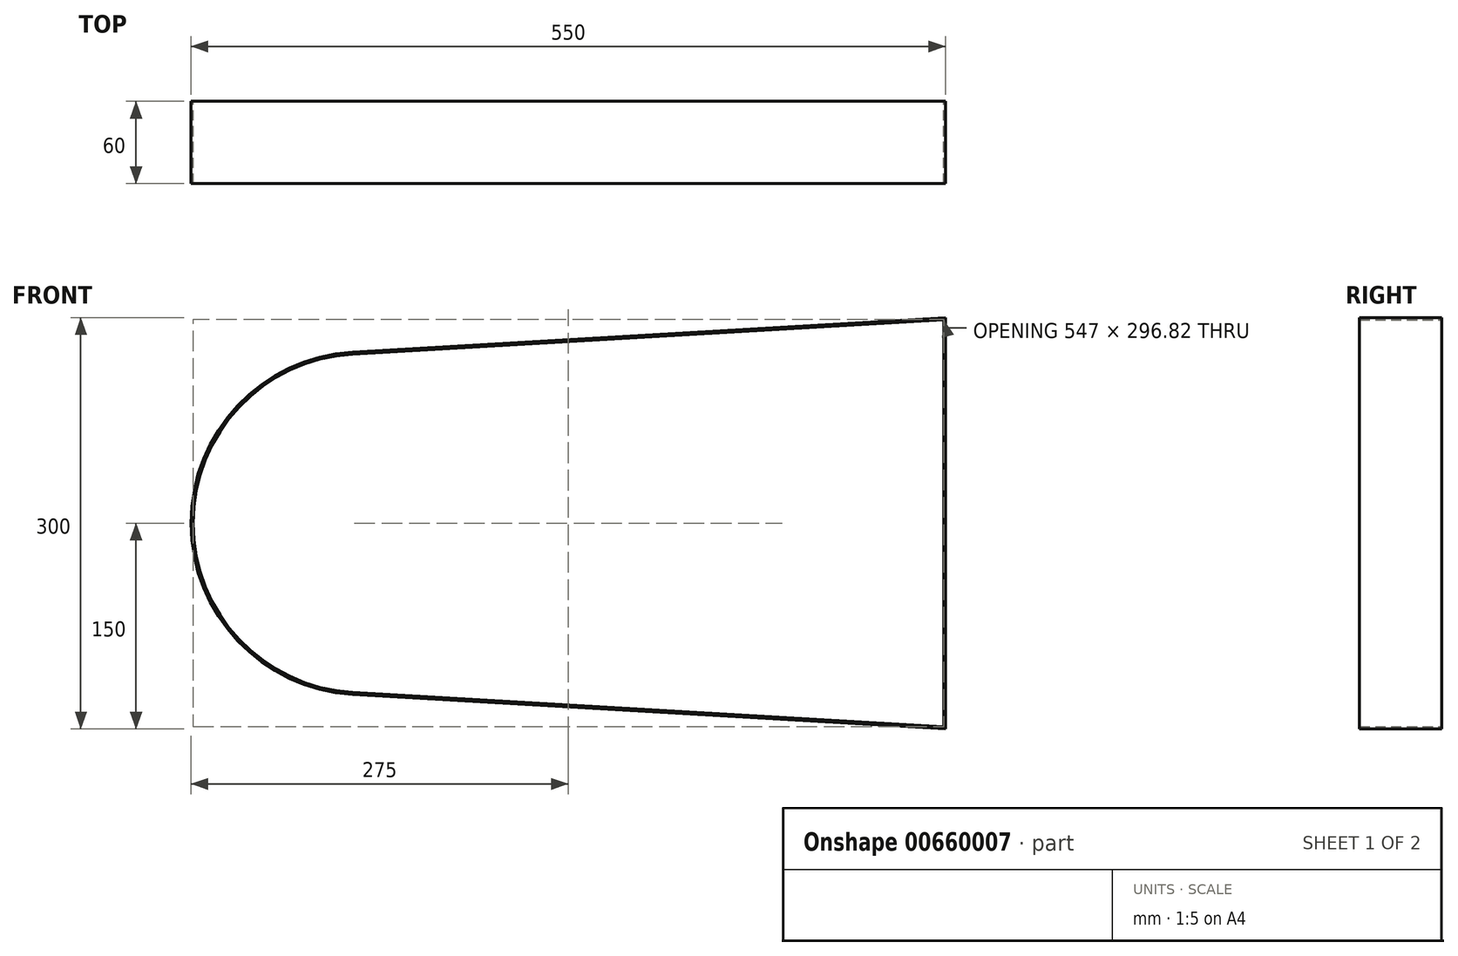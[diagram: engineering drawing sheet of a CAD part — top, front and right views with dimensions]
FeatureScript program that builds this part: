
annotation { "Feature Type Name" : "Feature", "Feature Type Description" : "" }
export const myFeature = defineFeature(function(context is Context, id is Id, definition is map)
    precondition{}
    {
        {
            var Q0;
            Q0=qCreatedBy(makeId("Front.planeOp"),FACE);
            var sketch = newSketch(context, id + "F0", { "sketchPlane" : qUnion([Q0])});
            skLineSegment(sketch, "E0", {"start": v(0, 0) * mm, "end": v(-425, 0) * mm});
            skLineSegment(sketch, "E1", {"start": v(0, 150) * mm, "end": v(-432.28, 124.79) * mm});
            skLineSegment(sketch, "E2", {"start": v(0, -150) * mm, "end": v(-432.28, -124.79) * mm});
            skLineSegment(sketch, "E3", {"start": v(0, 0) * mm, "end": v(0, 150) * mm});
            skLineSegment(sketch, "E4", {"start": v(0, 0) * mm, "end": v(0, -150) * mm});
            skArc(sketch, "E5", {"start": v(-432.28, 124.79) * mm, "mid": v(-550, 0) * mm, "end": v(-432.28, -124.79) * mm});
            skArc(sketch, "E6.0", {"start": v(-432.2, 123.3) * mm, "mid": v(-548.5, 0) * mm, "end": v(-432.2, -123.3) * mm});
            skLineSegment(sketch, "E6.1", {"start": v(-1.5, 148.4) * mm, "end": v(-432.2, 123.3) * mm});
            skLineSegment(sketch, "E6.2", {"start": v(-1.5, -148.4) * mm, "end": v(-432.2, -123.3) * mm});
            skLineSegment(sketch, "E6.3", {"start": v(-1.5, 0) * mm, "end": v(-1.5, -148.4) * mm});
            skLineSegment(sketch, "E6.4", {"start": v(-1.5, 0) * mm, "end": v(-1.5, 148.4) * mm});
            skSolve(sketch);
        }
        {
            var Q0;
            Q0=makeQuery(id+"F0.imprint","IMPRINT",FACE,{"disambiguationData":[TD([[makeQuery(id+"F0.imprint","IMPRINT",EDGE,{"derivedFrom":sQuery(id+"F0.wireOp",EDGE,"E1")}),1.0]])]});
            extrude(context, id + "F1", {"entities" : qUnion([Q0]), "depth" : 60 * mm, "offsetDistance" : 25 * mm});
        }
    });
